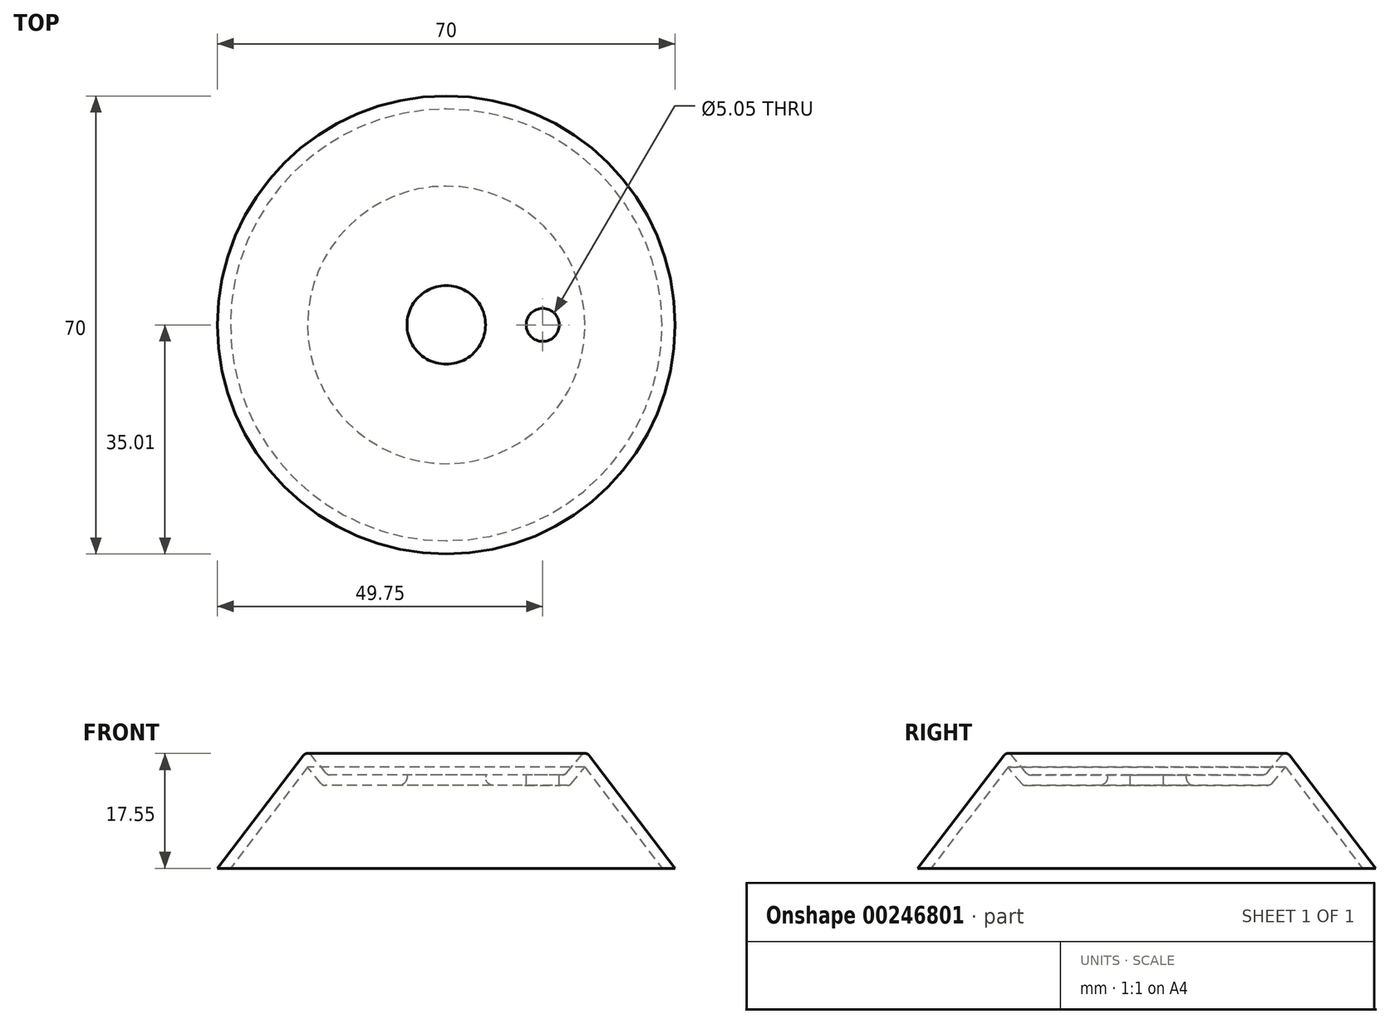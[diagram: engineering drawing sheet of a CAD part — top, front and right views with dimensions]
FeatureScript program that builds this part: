
annotation { "Feature Type Name" : "Feature", "Feature Type Description" : "" }
export const myFeature = defineFeature(function(context is Context, id is Id, definition is map)
    precondition{}
    {
        {
            var Q0;
            Q0=qCreatedBy(makeId("Front.planeOp"),FACE);
            var sketch = newSketch(context, id + "F0", { "sketchPlane" : qUnion([Q0])});
            skLineSegment(sketch, "E0", {"start": v(0, 0) * mm, "end": v(35, 0) * mm});
            skLineSegment(sketch, "E1", {"start": v(0, 0) * mm, "end": v(0, 18) * mm, "construction": true});
            skLineSegment(sketch, "E2", {"start": v(0, 18) * mm, "end": v(32.58, 18) * mm, "construction": true});
            skLineSegment(sketch, "E3", {"start": v(5.95, 0) * mm, "end": v(5.95, 14.28) * mm, "construction": true});
            skLineSegment(sketch, "E4", {"start": v(0, 14.28) * mm, "end": v(0, 0) * mm});
            skLineSegment(sketch, "E5", {"start": v(6.35, 0) * mm, "end": v(6.35, 13.76) * mm, "construction": true});
            skLineSegment(sketch, "E6", {"start": v(18.15, 0) * mm, "end": v(18.15, 18.32) * mm, "construction": true});
            skLineSegment(sketch, "E7", {"start": v(5.95, 14.28) * mm, "end": v(18.15, 14.28) * mm});
            skLineSegment(sketch, "E8", {"start": v(5.95, 14.28) * mm, "end": v(0, 14.28) * mm});
            skLineSegment(sketch, "E9", {"start": v(0, 14.28) * mm, "end": v(0, 14.28) * mm});
            skLineSegment(sketch, "E10", {"start": v(18.15, 14.28) * mm, "end": v(21.27, 18) * mm});
            skLineSegment(sketch, "E11", {"start": v(21.27, 18) * mm, "end": v(35, 0) * mm});
            skSolve(sketch);
        }
        {
            var Q0;
            Q0=qSketchRegion(id+"F0",true);
            extrude(context, id + "F1", {"entities" : qUnion([Q0]), "depth" : 0.01 * mm});
        }
        {
            var Q0;
            Q0=makeQuery(id+"F1.opExtrude","CAP_FACE",FACE,{"disambiguationData":[OSD([sQuery(id+"F0.wireOp",EDGE,"E0"),sQuery(id+"F0.wireOp",EDGE,"6y4ub3ka-Ihgj-H0nH-vjQd-nl8F7qjLXdH2"),sQuery(id+"F0.wireOp",EDGE,"k02bPiOn-f1VR-HTtH-kJtN-WkPaZOF7wZD0"),sQuery(id+"F0.wireOp",EDGE,"ieqvGgUx-12EA-STK7-xuCT-3rcJsafOrvBf"),sQuery(id+"F0.wireOp",EDGE,"E4")])],"isStart":false});
            var Q1;
            Q1=makeQuery(id+"F1.opExtrude","CAP_EDGE",EDGE,{"disambiguationData":[OSD([sQuery(id+"F0.wireOp",EDGE,"E4")])],"isStart":false});
            revolve(context, id + "F2", {"operationType" : NewBodyOperationType.ADD, "entities" : qUnion([Q0]), "axis" : qUnion([Q1]), "revolveType" : RevolveType.FULL});
        }
        {
            var Q0;
            {var subQ0=sQuery(id+"F0.wireOp",EDGE,"E0");Q0=makeQuery(id+"F2.boolean.opBoolean","MERGE",FACE,{"derivedFrom":[makeQuery(id+"F1.opExtrude","SWEPT_FACE",FACE,{"disambiguationData":[OSD([subQ0])]}),makeQuery(id+"F2.opRevolve","SWEPT_FACE",FACE,{"disambiguationData":[OSD([subQ0])]})]});}
            shell(context, id + "F3", {"entities" : qUnion([Q0]), "thickness" : 1.6 * mm});
        }
        {
            var Q0;
            {var subQ0=sQuery(id+"F0.wireOp",EDGE,"E0");Q0=makeQuery(id+"F2.boolean.opBoolean","MERGE",FACE,{"derivedFrom":[makeQuery(id+"F1.opExtrude","SWEPT_FACE",FACE,{"disambiguationData":[OSD([subQ0])]}),makeQuery(id+"F2.opRevolve","SWEPT_FACE",FACE,{"disambiguationData":[OSD([subQ0])]})]});}
            var sketch = newSketch(context, id + "F4", { "sketchPlane" : qUnion([Q0])});
            skCircle(sketch, "E12", {"center": v(0, 0.01) * mm, "radius": 6 * mm});
            skCircle(sketch, "E13", {"center": v(0, 0) * mm, "radius": 6 * mm});
            skSolve(sketch);
        }
        {
            var Q0;
            Q0=qSketchRegion(id+"F4",true);
            extrude(context, id + "F5", {"entities" : qUnion([Q0]), "operationType" : NewBodyOperationType.REMOVE, "oppositeDirection" : true, "depth" : 25 * mm});
        }
        {
            var Q0;
            Q0=makeQuery(id+"F2.opRevolve","SWEPT_EDGE",EDGE,{"disambiguationData":[OSD([sQuery(id+"F0.wireOp",EDGE,"i9SMpdhX-wvvY-t68j-uvlp-M6atMLKetHad"),sQuery(id+"F0.wireOp",EDGE,"nQEzmBRy-utbv-yRns-fLHs-DP6wbvmXK7bY")])]});
            var Q1;
            Q1=makeQuery(id+"F2.opRevolve","SWEPT_EDGE",EDGE,{"disambiguationData":[OSD([sQuery(id+"F0.wireOp",EDGE,"E7"),sQuery(id+"F0.wireOp",EDGE,"nQEzmBRy-utbv-yRns-fLHs-DP6wbvmXK7bY")])]});
            var Q2;
            {var subQ0=sQuery(id+"F0.wireOp",EDGE,"nQEzmBRy-utbv-yRns-fLHs-DP6wbvmXK7bY");var subQ1=sQuery(id+"F0.wireOp",EDGE,"E7");Q2=makeQuery(id+"F3.opShell","OFFSET_EDGE",EDGE,{"disambiguationData":[OSD([subQ1,subQ0]),TDD([makeQuery(id+"F2.opRevolve","SWEPT_EDGE",EDGE,{"disambiguationData":[OSD([subQ1,subQ0])]})])]});}
            var Q3;
            {var subQ0=sQuery(id+"F0.wireOp",EDGE,"nQEzmBRy-utbv-yRns-fLHs-DP6wbvmXK7bY");var subQ1=sQuery(id+"F0.wireOp",EDGE,"i9SMpdhX-wvvY-t68j-uvlp-M6atMLKetHad");Q3=makeQuery(id+"F3.opShell","OFFSET_EDGE",EDGE,{"disambiguationData":[OSD([subQ1,subQ0]),TDD([makeQuery(id+"F2.opRevolve","SWEPT_EDGE",EDGE,{"disambiguationData":[OSD([subQ1,subQ0])]})])]});}
            var Q4;
            Q4=makeQuery(id+"F2.opRevolve","SWEPT_EDGE",EDGE,{"disambiguationData":[OSD([sQuery(id+"F0.wireOp",EDGE,"E10"),sQuery(id+"F0.wireOp",EDGE,"E11")])]});
            fillet(context, id + "F6", {"entities" : qUnion([Q0, Q1, Q2, Q3, Q4]), "radius" : 0.75 * mm, "tangentPropagation" : true, "allowEdgeOverflow" : false});
        }
        {
            var Q0;
            Q0=makeQuery(id+"F5.boolean.opBoolean","INTERSECT",EDGE,{"derivedFrom":[makeQuery(id+"F3.opShell","OFFSET_FACE",FACE,{"disambiguationData":[OSD([sQuery(id+"F0.wireOp",EDGE,"E7"),sQuery(id+"F0.wireOp",EDGE,"E8")])]}),makeQuery(id+"F5.opExtrude","SWEPT_FACE",FACE,{"disambiguationData":[OSD([sQuery(id+"F4.wireOp",EDGE,"E12")])]})]});
            var Q1;
            Q1=makeQuery(id+"F5.boolean.opBoolean","INTERSECT",EDGE,{"derivedFrom":[makeQuery(id+"F3.opShell","OFFSET_FACE",FACE,{"disambiguationData":[OSD([sQuery(id+"F0.wireOp",EDGE,"E7"),sQuery(id+"F0.wireOp",EDGE,"E8")])]}),makeQuery(id+"F5.opExtrude","SWEPT_FACE",FACE,{"disambiguationData":[OSD([sQuery(id+"F4.wireOp",EDGE,"E13")])]})]});
            fillet(context, id + "F7", {"entities" : qUnion([Q0, Q1]), "radius" : 1.25 * mm, "tangentPropagation" : true, "allowEdgeOverflow" : false});
        }
        {
            var Q0;
            {var subQ0=sQuery(id+"F0.wireOp",EDGE,"E8");var subQ1=sQuery(id+"F0.wireOp",EDGE,"E7");Q0=makeQuery(id+"F2.boolean.opBoolean","MERGE",FACE,{"derivedFrom":[makeQuery(id+"F1.opExtrude","SWEPT_FACE",FACE,{"disambiguationData":[OSD([subQ1,subQ0])]}),makeQuery(id+"F2.opRevolve","SWEPT_FACE",FACE,{"disambiguationData":[OSD([subQ1,subQ0])]})]});}
            var sketch = newSketch(context, id + "F8", { "sketchPlane" : qUnion([Q0])});
            skLineSegment(sketch, "E14", {"start": v(0, 0) * mm, "end": v(14.75, 0) * mm, "construction": true});
            skCircle(sketch, "E15", {"center": v(14.75, 0) * mm, "radius": 2.52 * mm});
            skSolve(sketch);
        }
        {
            var Q0;
            Q0=makeQuery(id+"F8.imprint","IMPRINT",FACE,{"disambiguationData":[TD([[makeQuery(id+"F8.imprint","IMPRINT",EDGE,{"derivedFrom":sQuery(id+"F8.wireOp",EDGE,"E15")}),1.0]])]});
            var Q1;
            Q1=qConstructionFilter(qBodyType(qCreatedBy(id+"F8",EDGE),BodyType.WIRE),ConstructionObject.NO);
            extrude(context, id + "F9", {"entities" : qUnion([Q0]), "operationType" : NewBodyOperationType.REMOVE, "surfaceEntities" : qUnion([Q1]), "oppositeDirection" : true, "depth" : 25 * mm});
        }
        {
            var Q0;
            Q0=makeQuery(id+"F9.boolean.opBoolean","COPY",EDGE,{"derivedFrom":makeQuery(id+"F9.opExtrude","CAP_EDGE",EDGE,{"disambiguationData":[OSD([sQuery(id+"F8.wireOp",EDGE,"E15")])],"isStart":true})});
            var Q1;
            Q1=makeQuery(id+"F9.boolean.opBoolean","INTERSECT",EDGE,{"derivedFrom":[makeQuery(id+"F3.opShell","OFFSET_FACE",FACE,{"disambiguationData":[OSD([sQuery(id+"F0.wireOp",EDGE,"E7"),sQuery(id+"F0.wireOp",EDGE,"E8")])]}),makeQuery(id+"F9.opExtrude","SWEPT_FACE",FACE,{"disambiguationData":[OSD([sQuery(id+"F8.wireOp",EDGE,"E15")])]})]});
            fillet(context, id + "F10", {"entities" : qUnion([Q0, Q1]), "radius" : 0.2 * mm, "tangentPropagation" : true, "allowEdgeOverflow" : false});
        }
    });
